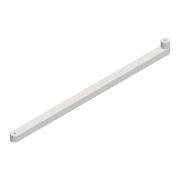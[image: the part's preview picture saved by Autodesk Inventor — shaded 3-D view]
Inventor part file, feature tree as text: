
AUTODESK INVENTOR PART (.ipt)
format: ipt  version: 2022 (Build 260153000, 153)  size: 100,864 bytes
history: native  units: mm
features: extrude x2, sketch x2, projected_geometry x1
ambient origin geometry x8: Origin, YZ Plane, XZ Plane, XY Plane, X Axis, Y Axis, Z Axis, Center Point
bodies: Solid1 (feature_tree)
feature tree (5):
  extrude  "Extrusion1"  Depth=10.0mm
  extrude  "Extrusion2"  Depth=8.0mm
  sketch  "Sketch1"  dims[d0=225.149mm d1=10.0mm]
  sketch  "Sketch2"  dims[d2=3.0mm d3=3.0mm d4=8.0mm d5=0.0mm d12=10.0mm d13=8.0mm d14=0.0mm]
  projected_geometry  "Projected Loop1"
